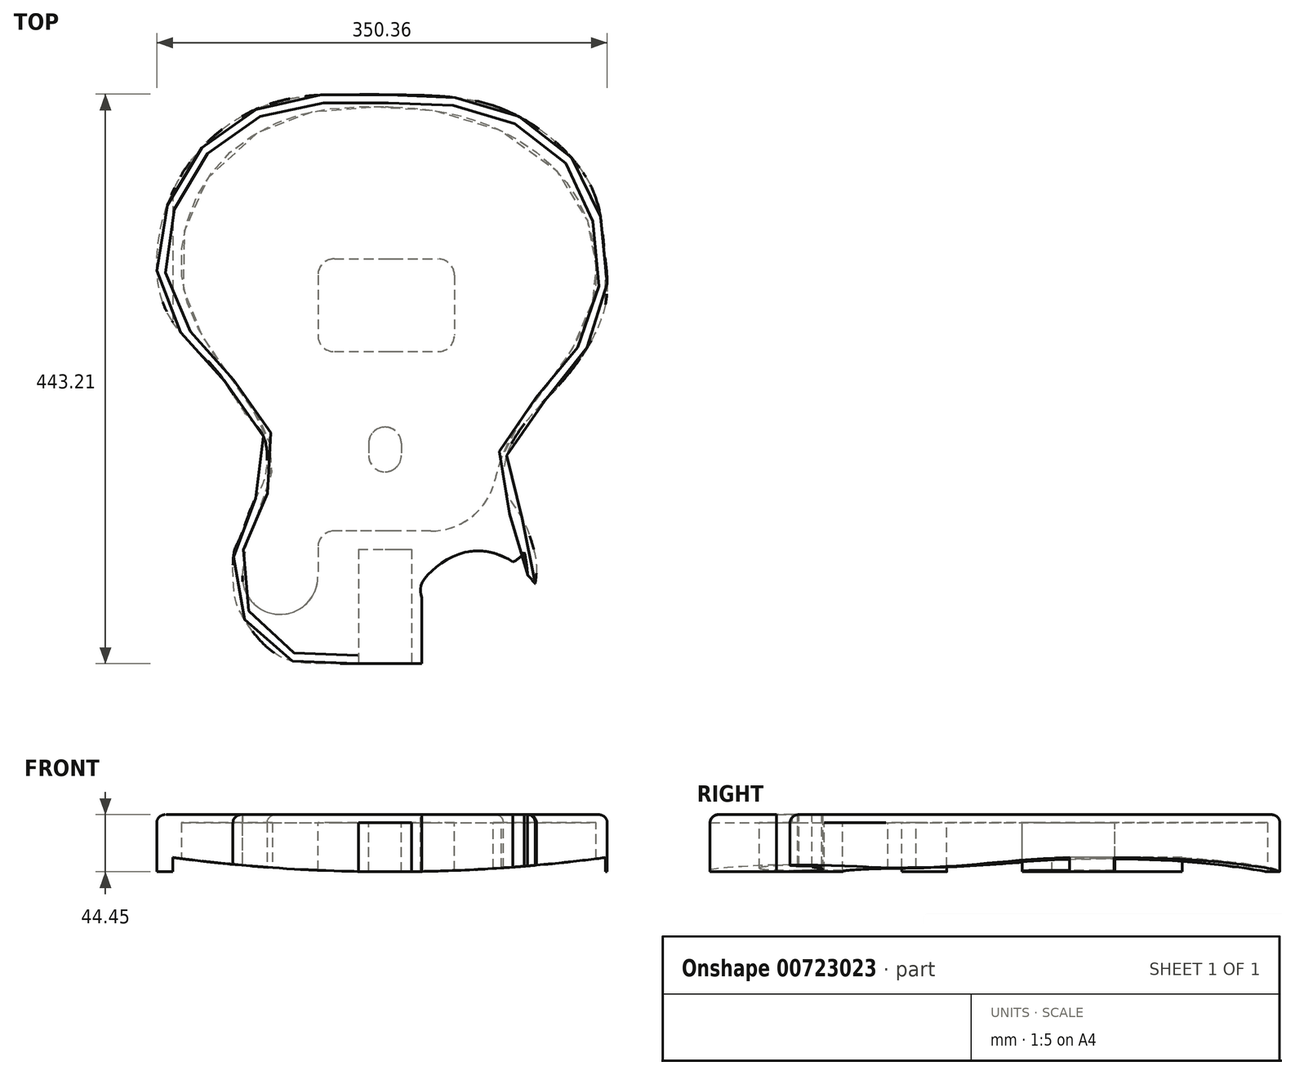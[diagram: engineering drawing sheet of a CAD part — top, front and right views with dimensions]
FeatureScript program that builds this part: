
annotation { "Feature Type Name" : "Feature", "Feature Type Description" : "" }
export const myFeature = defineFeature(function(context is Context, id is Id, definition is map)
    precondition{}
    {
        {
            var Q0;
            Q0=qCreatedBy(makeId("Top.planeOp"),FACE);
            var sketch = newSketch(context, id + "F0", { "sketchPlane" : qUnion([Q0])});
            skFitSpline(sketch, "E0.0", {"points": [v(24.97, -130.68) * mm, v(24.97, -119.75) * mm, v(57.94, -95.86) * mm, v(94.63, -102.44) * mm, v(113.09, -120.18) * mm]});
            skFitSpline(sketch, "E0.1", {"points": [v(-25.03, -182.34) * mm, v(-52.62, -182.34) * mm, v(-87.85, -175.37) * mm, v(-116.14, -142.47) * mm, v(-121.04, -126.28) * mm, v(-121.13, -95.89) * mm, v(-116.63, -84.8) * mm, v(-106.4, -57.9) * mm, v(-97.1, -37.63) * mm, v(-98.08, -5.8) * mm, v(-110.9, 10.46) * mm, v(-135.48, 46.75) * mm, v(-175.53, 96) * mm, v(-165.66, 191.54) * mm, v(-93.42, 253.17) * mm, v(-2.38, 260.37) * mm, v(87.68, 249.3) * mm, v(155.19, 191.74) * mm, v(166.79, 140.27) * mm, v(167.1, 94.3) * mm, v(140.89, 45.49) * mm, v(118.15, 20.01) * mm, v(91.56, -18.26) * mm, v(90.84, -49.26) * mm, v(102.29, -68.12) * mm, v(113.26, -99.56) * mm, v(113.87, -113.65) * mm, v(113.09, -120.18) * mm]});
            skLineSegment(sketch, "E0.2", {"start": v(-24.37, -182.34) * mm, "end": v(16.9, -182.34) * mm});
            skLineSegment(sketch, "E0.3", {"start": v(16.9, -182.34) * mm, "end": v(24.97, -182.34) * mm});
            skLineSegment(sketch, "E0.4", {"start": v(24.97, -182.34) * mm, "end": v(24.97, -130.68) * mm});
            skFitSpline(sketch, "E1.0", {"points": [v(-25.03, -176) * mm, v(-31.98, -176) * mm, v(-42.6, -175.41) * mm, v(-56.36, -173.25) * mm, v(-66.3, -170.9) * mm, v(-75.64, -167.76) * mm, v(-82.78, -164.47) * mm, v(-88.02, -161.43) * mm, v(-91.69, -158.94) * mm, v(-94.52, -156.69) * mm, v(-96.64, -154.78) * mm, v(-98.17, -153.28) * mm, v(-99.64, -151.73) * mm, v(-101.05, -150.13) * mm, v(-102.4, -148.5) * mm, v(-103.66, -146.86) * mm, v(-104.86, -145.22) * mm, v(-106.33, -143.06) * mm, v(-107.96, -140.38) * mm, v(-109.61, -137.19) * mm, v(-111, -133.97) * mm, v(-112.13, -130.69) * mm, v(-113.04, -127.29) * mm, v(-113.74, -123.74) * mm, v(-114.25, -119.99) * mm, v(-114.52, -116.67) * mm, v(-114.64, -113.88) * mm, v(-114.7, -111.75) * mm, v(-114.7, -109.63) * mm, v(-114.66, -107.55) * mm, v(-114.58, -105.56) * mm, v(-114.4, -103.05) * mm, v(-114.06, -100.13) * mm, v(-113.5, -96.87) * mm, v(-112.75, -93.72) * mm, v(-111.84, -90.56) * mm, v(-110.75, -87.3) * mm, v(-109.7, -84.4) * mm, v(-108.77, -81.94) * mm, v(-108.03, -80.01) * mm, v(-107.26, -78) * mm, v(-106.17, -75.17) * mm, v(-105.04, -72.2) * mm, v(-103.84, -69.16) * mm, v(-102.6, -66.08) * mm, v(-100.97, -62.07) * mm, v(-98.95, -57.1) * mm, v(-96.97, -51.98) * mm, v(-95.12, -46.74) * mm, v(-93.78, -42.3) * mm, v(-92.87, -38.72) * mm, v(-92.29, -36) * mm, v(-91.9, -33.74) * mm, v(-91.64, -31.91) * mm, v(-91.5, -30.54) * mm, v(-91.37, -29.17) * mm, v(-91.27, -27.35) * mm, v(-91.22, -25.12) * mm, v(-91.3, -22.5) * mm, v(-91.54, -19.1) * mm, v(-92.1, -15.04) * mm, v(-93.15, -10.43) * mm, v(-94.5, -6.06) * mm, v(-96.14, -1.93) * mm, v(-98.62, 3.3) * mm, v(-101.45, 8.15) * mm, v(-104.46, 12.75) * mm, v(-106.78, 16.11) * mm, v(-108.73, 18.86) * mm, v(-110.27, 21.05) * mm, v(-111.43, 22.69) * mm, v(-112.58, 24.34) * mm, v(-114.12, 26.57) * mm, v(-116.07, 29.4) * mm, v(-118.06, 32.28) * mm, v(-119.68, 34.6) * mm, v(-121.32, 36.93) * mm, v(-123.4, 39.84) * mm, v(-126.72, 44.48) * mm, v(-130.9, 50.3) * mm, v(-135.86, 57.3) * mm, v(-140.63, 64.38) * mm, v(-145.13, 71.54) * mm, v(-149.27, 78.8) * mm, v(-152.94, 86.2) * mm, v(-155.55, 92.47) * mm, v(-157.32, 97.57) * mm, v(-158.87, 102.75) * mm, v(-160.4, 109.38) * mm, v(-161.62, 117.54) * mm, v(-162.2, 125.83) * mm, v(-162.15, 134.2) * mm, v(-161.27, 145.39) * mm, v(-159.17, 156.5) * mm, v(-155.9, 167.28) * mm, v(-152.86, 175.15) * mm, v(-149.27, 182.74) * mm, v(-145.13, 190.01) * mm, v(-140.45, 196.96) * mm, v(-133.56, 205.76) * mm, v(-123.82, 215.85) * mm, v(-112.85, 224.56) * mm, v(-103.48, 230.62) * mm, v(-96.2, 234.7) * mm, v(-88.72, 238.27) * mm, v(-81.08, 241.32) * mm, v(-73.26, 243.89) * mm, v(-62.63, 246.7) * mm, v(-48.97, 249.18) * mm, v(-34.94, 250.5) * mm, v(-23.58, 251) * mm, v(-16.43, 251.12) * mm, v(-10.69, 251.11) * mm, v(-4.94, 251.05) * mm, v(2.22, 250.86) * mm, v(10.78, 250.43) * mm, v(22.12, 249.57) * mm, v(36.12, 247.87) * mm, v(52.58, 244.64) * mm, v(65.94, 240.8) * mm, v(76.37, 236.93) * mm, v(84.06, 233.62) * mm, v(91.62, 229.86) * mm, v(101.47, 224.27) * mm, v(113.24, 216.24) * mm, v(126.07, 205.13) * mm, v(135.38, 194.79) * mm, v(141.8, 185.96) * mm, v(146.08, 179.07) * mm, v(149.76, 171.96) * mm, v(152.85, 164.59) * mm, v(155.4, 156.97) * mm, v(157.4, 149.13) * mm, v(158.66, 142.43) * mm, v(159.42, 136.98) * mm, v(159.87, 132.86) * mm, v(160.15, 129.39) * mm, v(160.32, 126.6) * mm, v(160.45, 123.8) * mm, v(160.53, 120.33) * mm, v(160.47, 116.9) * mm, v(160.31, 114.17) * mm, v(160.08, 111.46) * mm, v(159.64, 108.04) * mm, v(158.87, 103.9) * mm, v(157.9, 99.74) * mm, v(156.72, 95.57) * mm, v(154.92, 90.02) * mm, v(152.25, 83.15) * mm, v(148.57, 75.11) * mm, v(144.54, 67.41) * mm, v(141.03, 61.37) * mm, v(138.22, 56.8) * mm, v(136.13, 53.54) * mm, v(134.07, 50.45) * mm, v(131.38, 46.52) * mm, v(128.06, 41.9) * mm, v(124.02, 36.54) * mm, v(119.8, 31.08) * mm, v(116.03, 26.24) * mm, v(112.82, 22.07) * mm, v(110.3, 18.76) * mm, v(108.1, 15.82) * mm, v(106.26, 13.36) * mm, v(104.38, 10.8) * mm, v(101.93, 7.4) * mm, v(98.95, 3.03) * mm, v(96, -1.63) * mm, v(93.2, -6.57) * mm, v(90.62, -11.77) * mm, v(88.39, -17.25) * mm, v(86.59, -23) * mm, v(85.55, -28) * mm, v(85.05, -32.13) * mm, v(84.87, -35.3) * mm, v(84.9, -38) * mm, v(85.04, -40.19) * mm, v(85.21, -41.84) * mm, v(85.45, -43.49) * mm, v(85.85, -45.66) * mm, v(86.47, -48.34) * mm, v(87.4, -51.5) * mm, v(88.83, -55.64) * mm, v(90.9, -60.7) * mm, v(93.6, -66.64) * mm, v(95.86, -71.48) * mm, v(97.58, -75.28) * mm, v(98.8, -78.1) * mm, v(99.92, -80.87) * mm, v(100.95, -83.64) * mm, v(101.9, -86.4) * mm, v(103.04, -90) * mm, v(104.24, -94.29) * mm, v(105.34, -99.1) * mm, v(106.14, -103.55) * mm, v(106.85, -108.97) * mm, v(107.1, -113.57) * mm, v(107, -117.26) * mm, v(106.86, -118.77) * mm, v(106.78, -119.43) * mm]});
            skLineSegment(sketch, "E2", {"start": v(-3.73, 257.36) * mm, "end": v(-3.73, 314.5) * mm, "construction": true});
            skFitSpline(sketch, "E3.trimOffspring", {"points": [v(-25.03, -176) * mm, v(-31.98, -176) * mm, v(-42.6, -175.41) * mm, v(-56.36, -173.25) * mm, v(-66.3, -170.9) * mm, v(-75.64, -167.76) * mm, v(-82.78, -164.47) * mm, v(-88.02, -161.43) * mm, v(-91.69, -158.94) * mm, v(-94.52, -156.69) * mm, v(-96.64, -154.78) * mm, v(-98.17, -153.28) * mm, v(-99.64, -151.73) * mm, v(-101.05, -150.13) * mm, v(-102.4, -148.5) * mm, v(-103.66, -146.86) * mm, v(-104.86, -145.22) * mm, v(-106.33, -143.06) * mm, v(-107.96, -140.38) * mm, v(-109.61, -137.19) * mm, v(-111, -133.97) * mm, v(-112.13, -130.69) * mm, v(-113.04, -127.29) * mm, v(-113.74, -123.74) * mm, v(-114.25, -119.99) * mm, v(-114.52, -116.67) * mm, v(-114.64, -113.88) * mm, v(-114.7, -111.75) * mm, v(-114.7, -109.63) * mm, v(-114.66, -107.55) * mm, v(-114.58, -105.56) * mm, v(-114.4, -103.05) * mm, v(-114.06, -100.13) * mm, v(-113.5, -96.87) * mm, v(-112.75, -93.72) * mm, v(-111.84, -90.56) * mm, v(-110.75, -87.3) * mm, v(-109.7, -84.4) * mm, v(-108.77, -81.94) * mm, v(-108.03, -80.01) * mm, v(-107.26, -78) * mm, v(-106.17, -75.17) * mm, v(-105.04, -72.2) * mm, v(-103.84, -69.16) * mm, v(-102.6, -66.08) * mm, v(-100.97, -62.07) * mm, v(-98.95, -57.1) * mm, v(-96.97, -51.98) * mm, v(-95.12, -46.74) * mm, v(-93.78, -42.3) * mm, v(-92.87, -38.72) * mm, v(-92.29, -36) * mm, v(-91.9, -33.74) * mm, v(-91.64, -31.91) * mm, v(-91.5, -30.54) * mm, v(-91.37, -29.17) * mm, v(-91.27, -27.35) * mm, v(-91.22, -25.12) * mm, v(-91.3, -22.5) * mm, v(-91.54, -19.1) * mm, v(-92.1, -15.04) * mm, v(-93.15, -10.43) * mm, v(-94.5, -6.06) * mm, v(-96.14, -1.93) * mm, v(-98.62, 3.3) * mm, v(-101.45, 8.15) * mm, v(-104.46, 12.75) * mm, v(-106.78, 16.11) * mm, v(-108.73, 18.86) * mm, v(-110.27, 21.05) * mm, v(-111.43, 22.69) * mm, v(-112.58, 24.34) * mm, v(-114.12, 26.57) * mm, v(-116.07, 29.4) * mm, v(-118.06, 32.28) * mm, v(-119.68, 34.6) * mm, v(-121.32, 36.93) * mm, v(-123.4, 39.84) * mm, v(-126.72, 44.48) * mm, v(-130.9, 50.3) * mm, v(-135.86, 57.3) * mm, v(-140.63, 64.38) * mm, v(-145.13, 71.54) * mm, v(-149.27, 78.8) * mm, v(-152.94, 86.2) * mm, v(-155.55, 92.47) * mm, v(-157.32, 97.57) * mm, v(-158.87, 102.75) * mm, v(-160.4, 109.38) * mm, v(-161.62, 117.54) * mm, v(-162.2, 125.83) * mm, v(-162.15, 134.2) * mm, v(-161.27, 145.39) * mm, v(-159.17, 156.5) * mm, v(-155.9, 167.28) * mm, v(-152.86, 175.15) * mm, v(-149.27, 182.74) * mm, v(-145.13, 190.01) * mm, v(-140.45, 196.96) * mm, v(-133.56, 205.76) * mm, v(-123.82, 215.85) * mm, v(-112.85, 224.56) * mm, v(-103.48, 230.62) * mm, v(-96.2, 234.7) * mm, v(-88.72, 238.27) * mm, v(-81.08, 241.32) * mm, v(-73.26, 243.89) * mm, v(-62.63, 246.7) * mm, v(-48.97, 249.18) * mm, v(-34.94, 250.5) * mm, v(-23.58, 251) * mm, v(-16.43, 251.12) * mm, v(-10.69, 251.11) * mm, v(-4.94, 251.05) * mm, v(2.22, 250.86) * mm, v(10.78, 250.43) * mm, v(22.12, 249.57) * mm, v(36.12, 247.87) * mm, v(52.58, 244.64) * mm, v(65.94, 240.8) * mm, v(76.37, 236.93) * mm, v(84.06, 233.62) * mm, v(91.62, 229.86) * mm, v(101.47, 224.27) * mm, v(113.24, 216.24) * mm, v(126.07, 205.13) * mm, v(135.38, 194.79) * mm, v(141.8, 185.96) * mm, v(146.08, 179.07) * mm, v(149.76, 171.96) * mm, v(152.85, 164.59) * mm, v(155.4, 156.97) * mm, v(157.4, 149.13) * mm, v(158.66, 142.43) * mm, v(159.42, 136.98) * mm, v(159.87, 132.86) * mm, v(160.15, 129.39) * mm, v(160.32, 126.6) * mm, v(160.45, 123.8) * mm, v(160.53, 120.33) * mm, v(160.47, 116.9) * mm, v(160.31, 114.17) * mm, v(160.08, 111.46) * mm, v(159.64, 108.04) * mm, v(158.87, 103.9) * mm, v(157.9, 99.74) * mm, v(156.72, 95.57) * mm, v(154.92, 90.02) * mm, v(152.25, 83.15) * mm, v(148.57, 75.11) * mm, v(144.54, 67.41) * mm, v(141.03, 61.37) * mm, v(138.22, 56.8) * mm, v(136.13, 53.54) * mm, v(134.07, 50.45) * mm, v(131.38, 46.52) * mm, v(128.06, 41.9) * mm, v(124.02, 36.54) * mm, v(119.8, 31.08) * mm, v(116.03, 26.24) * mm, v(112.82, 22.07) * mm, v(110.3, 18.76) * mm, v(108.1, 15.82) * mm, v(106.26, 13.36) * mm, v(104.38, 10.8) * mm, v(101.93, 7.4) * mm, v(98.95, 3.03) * mm, v(96, -1.63) * mm, v(93.2, -6.57) * mm, v(90.62, -11.77) * mm, v(88.39, -17.25) * mm, v(86.59, -23) * mm, v(85.55, -28) * mm, v(85.05, -32.13) * mm, v(84.87, -35.3) * mm, v(84.9, -38) * mm, v(85.04, -40.19) * mm, v(85.21, -41.84) * mm, v(85.45, -43.49) * mm, v(85.85, -45.66) * mm, v(86.47, -48.34) * mm, v(87.4, -51.5) * mm, v(88.83, -55.64) * mm, v(90.9, -60.7) * mm, v(93.6, -66.64) * mm, v(95.86, -71.48) * mm, v(97.58, -75.28) * mm, v(98.8, -78.1) * mm, v(99.92, -80.87) * mm, v(100.95, -83.64) * mm, v(101.9, -86.4) * mm, v(103.04, -90) * mm, v(104.24, -94.29) * mm, v(105.34, -99.1) * mm, v(106.14, -103.55) * mm, v(106.85, -108.97) * mm, v(107.1, -113.57) * mm, v(107, -117.26) * mm, v(106.86, -118.77) * mm, v(106.78, -119.43) * mm]});
            skArc(sketch, "E4.trimOffspring", {"start": v(-38.74, 246.82) * mm, "mid": v(-5.23, 238.32) * mm, "end": v(28.6, 245.5) * mm});
            skPoint(sketch, "E5.visualSharp", {"position": v(33.55, 248.05) * mm});
            skArc(sketch, "E5.filletArc", {"start": v(39.99, 247.01) * mm, "mid": v(34.17, 247.14) * mm, "end": v(28.6, 245.5) * mm});
            skPoint(sketch, "E6.visualSharp", {"position": v(-43.64, 249.6) * mm});
            skArc(sketch, "E6.filletArc", {"start": v(-38.74, 246.82) * mm, "mid": v(-44.33, 248.69) * mm, "end": v(-50.21, 248.76) * mm});
            skArc(sketch, "E7.filletArc", {"start": v(83.94, -104.3) * mm, "mid": v(102.56, -98.18) * mm, "end": v(105.94, -78.87) * mm});
            skLineSegment(sketch, "E8", {"start": v(50.24, -15.3) * mm, "end": v(50.24, 47.77) * mm});
            skArc(sketch, "E9", {"start": v(-55.92, -114.66) * mm, "mid": v(-85.6, -144.02) * mm, "end": v(-114.63, -114.02) * mm});
            skLineSegment(sketch, "E10", {"start": v(-55.92, -114.66) * mm, "end": v(-55.92, -91.8) * mm});
            skLineSegment(sketch, "E11.0.1", {"start": v(50.24, 8.09) * mm, "end": v(-55.92, 8.09) * mm});
            skLineSegment(sketch, "E11.0.7", {"start": v(-55.92, 47.77) * mm, "end": v(50.24, 47.77) * mm});
            skLineSegment(sketch, "E11.1.4", {"start": v(32.86, 47.77) * mm, "end": v(32.86, 8.09) * mm});
            skLineSegment(sketch, "E11.2.2", {"start": v(-39.45, -39.42) * mm, "end": v(31.99, -39.42) * mm});
            skLineSegment(sketch, "E11.2.3", {"start": v(31.99, -39.42) * mm, "end": v(31.99, -79.1) * mm});
            skLineSegment(sketch, "E11.2.8", {"start": v(31.99, -79.1) * mm, "end": v(-43.22, -79.1) * mm});
            skLineSegment(sketch, "E11.3.3", {"start": v(-39.45, -79.1) * mm, "end": v(-39.45, -39.42) * mm});
            skLineSegment(sketch, "E12", {"start": v(-24.37, -182.34) * mm, "end": v(-25.03, -182.34) * mm});
            skLineSegment(sketch, "E13.0.0", {"start": v(-24.37, -93.44) * mm, "end": v(16.9, -93.44) * mm});
            skLineSegment(sketch, "E13.0.1", {"start": v(16.9, -93.44) * mm, "end": v(16.9, -182.34) * mm});
            skLineSegment(sketch, "E13.0.2", {"start": v(16.9, -182.34) * mm, "end": v(-24.37, -182.34) * mm});
            skLineSegment(sketch, "E13.0.3", {"start": v(-24.37, -182.34) * mm, "end": v(-24.37, -93.44) * mm});
            skLineSegment(sketch, "E14", {"start": v(-38.58, 47.77) * mm, "end": v(-38.58, 8.09) * mm});
            skLineSegment(sketch, "E15.0", {"start": v(-43.22, 132.64) * mm, "end": v(37.54, 132.64) * mm});
            skLineSegment(sketch, "E16.0", {"start": v(-43.22, 60.47) * mm, "end": v(37.54, 60.47) * mm});
            skLineSegment(sketch, "E17.trimOffspring", {"start": v(50.24, 73.17) * mm, "end": v(50.24, 119.94) * mm});
            skLineSegment(sketch, "E18.trimOffspring", {"start": v(-55.92, 73.17) * mm, "end": v(-55.92, 119.94) * mm});
            skPoint(sketch, "E19.visualSharp", {"position": v(-55.92, 132.64) * mm});
            skArc(sketch, "E19.filletArc", {"start": v(-43.22, 132.64) * mm, "mid": v(-52.2, 128.92) * mm, "end": v(-55.92, 119.94) * mm});
            skPoint(sketch, "E20.visualSharp", {"position": v(50.24, 132.64) * mm});
            skArc(sketch, "E20.filletArc", {"start": v(50.24, 119.94) * mm, "mid": v(46.52, 128.92) * mm, "end": v(37.54, 132.64) * mm});
            skPoint(sketch, "E21.visualSharp", {"position": v(50.24, 60.47) * mm});
            skArc(sketch, "E21.filletArc", {"start": v(37.54, 60.47) * mm, "mid": v(46.52, 64.2) * mm, "end": v(50.24, 73.17) * mm});
            skPoint(sketch, "E22.visualSharp", {"position": v(-55.92, 60.47) * mm});
            skArc(sketch, "E22.filletArc", {"start": v(-55.92, 73.17) * mm, "mid": v(-52.2, 64.2) * mm, "end": v(-43.22, 60.47) * mm});
            skLineSegment(sketch, "E23.0", {"start": v(-3.73, 1.74) * mm, "end": v(-3.73, 1.74) * mm});
            skLineSegment(sketch, "E24.0", {"start": v(-3.73, -33.07) * mm, "end": v(-3.73, -33.07) * mm});
            skLineSegment(sketch, "E25.0", {"start": v(8.97, -20.37) * mm, "end": v(8.97, -10.96) * mm});
            skLineSegment(sketch, "E26.0", {"start": v(-16.43, -20.37) * mm, "end": v(-16.43, -10.96) * mm});
            skPoint(sketch, "E27.visualSharp", {"position": v(-16.43, 1.74) * mm});
            skArc(sketch, "E27.filletArc", {"start": v(-3.73, 1.74) * mm, "mid": v(-12.71, -1.98) * mm, "end": v(-16.43, -10.96) * mm});
            skPoint(sketch, "E28.visualSharp", {"position": v(8.97, 1.74) * mm});
            skArc(sketch, "E28.filletArc", {"start": v(8.97, -10.96) * mm, "mid": v(5.25, -1.98) * mm, "end": v(-3.73, 1.74) * mm});
            skPoint(sketch, "E29.visualSharp", {"position": v(8.97, -33.07) * mm});
            skArc(sketch, "E29.filletArc", {"start": v(-3.73, -33.07) * mm, "mid": v(5.25, -29.35) * mm, "end": v(8.97, -20.37) * mm});
            skPoint(sketch, "E30.visualSharp", {"position": v(-16.43, -33.07) * mm});
            skArc(sketch, "E30.filletArc", {"start": v(-16.43, -20.37) * mm, "mid": v(-12.71, -29.35) * mm, "end": v(-3.73, -33.07) * mm});
            skArc(sketch, "E31", {"start": v(31.99, -79.1) * mm, "mid": v(61.88, -69.45) * mm, "end": v(80.47, -44.12) * mm});
            skArc(sketch, "E32", {"start": v(88.12, -18.25) * mm, "mid": v(84.02, -31.1) * mm, "end": v(80.47, -44.12) * mm});
            skArc(sketch, "E33.filletArc", {"start": v(-43.22, -79.1) * mm, "mid": v(-52.2, -82.83) * mm, "end": v(-55.92, -91.8) * mm});
            skSolve(sketch);
        }
        {
            var Q0;
            Q0=makeQuery(id+"F0.imprint","IMPRINT",FACE,{"disambiguationData":[TD([[makeQuery(id+"F0.imprint","IMPRINT",EDGE,{"derivedFrom":sQuery(id+"F0.wireOp",EDGE,"E0.0")}),1.0]])]});
            var Q1;
            Q1=makeQuery(id+"F0.imprint","IMPRINT",FACE,{"disambiguationData":[TD([[makeQuery(id+"F0.imprint","IMPRINT",EDGE,{"derivedFrom":sQuery(id+"F0.wireOp",EDGE,"E15.0")}),-1.0]])]});
            var Q2;
            Q2=makeQuery(id+"F0.imprint","IMPRINT",FACE,{"disambiguationData":[TD([[makeQuery(id+"F0.imprint","IMPRINT",EDGE,{"derivedFrom":sQuery(id+"F0.wireOp",EDGE,"E25.0")}),1.0]])]});
            extrude(context, id + "F1", {"entities" : qUnion([Q0, Q1, Q2]), "oppositeDirection" : true, "depth" : 44.45 * mm, "offsetDistance" : 25.4 * mm});
        }
        {
            var Q0;
            Q0=makeQuery(id+"F0.imprint","IMPRINT",FACE,{"disambiguationData":[TD([[makeQuery(id+"F0.imprint","IMPRINT",EDGE,{"derivedFrom":sQuery(id+"F0.wireOp",EDGE,"E1.0")}),-1.0]])]});
            var Q1;
            {var subQ0=sQuery(id+"F0.wireOp",EDGE,"E11.1.4");Q1=makeQuery(id+"F0.imprint","IMPRINT",FACE,{"disambiguationData":[TD([[makeQuery(id+"F0.imprint","IMPRINT",EDGE,{"derivedFrom":subQ0}),-1.0]])]});}
            var Q2;
            Q2=makeQuery(id+"F0.imprint","IMPRINT",FACE,{"disambiguationData":[TD([[makeQuery(id+"F0.imprint","IMPRINT",EDGE,{"derivedFrom":sQuery(id+"F0.wireOp",EDGE,"E11.2.2")}),-1.0]])]});
            var Q3;
            {var subQ5=sQuery(id+"F0.wireOp",EDGE,"E11.1.4");Q3=makeQuery(id+"F0.imprint","IMPRINT",FACE,{"disambiguationData":[TD([[makeQuery(id+"F0.imprint","IMPRINT",EDGE,{"derivedFrom":subQ5}),1.0]])]});}
            var Q4;
            Q4=makeQuery(id+"F0.imprint","IMPRINT",FACE,{"disambiguationData":[TD([[makeQuery(id+"F0.imprint","IMPRINT",EDGE,{"derivedFrom":sQuery(id+"F0.wireOp",EDGE,"E13.0.0")}),-1.0]])]});
            extrude(context, id + "F2", {"entities" : qUnion([Q0, Q1, Q2, Q3, Q4]), "operationType" : NewBodyOperationType.ADD, "oppositeDirection" : true, "depth" : 6.35 * mm, "offsetDistance" : 25.4 * mm});
        }
        {
            var Q0;
            Q0=makeQuery(id+"F1.opExtrude","CAP_EDGE",EDGE,{"disambiguationData":[OSD([sQuery(id+"F0.wireOp",EDGE,"E0.1")])],"isStart":true});
            fillet(context, id + "F3", {"entities" : qUnion([Q0]), "radius" : 6.35 * mm, "tangentPropagation" : true, "allowEdgeOverflow" : false});
        }
        {
            var Q0;
            Q0=makeQuery(id+"F1.opExtrude","SWEPT_FACE",FACE,{"disambiguationData":[OSD([sQuery(id+"F0.wireOp",EDGE,"E13.0.0")])]});
            cPlane(context, id + "F4", {"entities" : qUnion([Q0]), "cplaneType" : CPlaneType.OFFSET, "offset" : 101.6 * mm, "width" : 152.4 * mm, "height" : 152.4 * mm});
        }
        {
            var Q0;
            Q0=qCreatedBy(id+"F4.planeOp",FACE);
            var sketch = newSketch(context, id + "F5", { "sketchPlane" : qUnion([Q0])});
            skLineSegment(sketch, "E34", {"start": v(-3.73, -44.45) * mm, "end": v(-3.73, -102.59) * mm, "construction": true});
            skLineSegment(sketch, "E35", {"start": v(-3.73, -44.45) * mm, "end": v(-3.73, -33.34) * mm, "construction": true});
            skLineSegment(sketch, "E36", {"start": v(-3.73, -33.34) * mm, "end": v(167.72, -33.34) * mm, "construction": true});
            skLineSegment(sketch, "E37", {"start": v(-3.73, -33.34) * mm, "end": v(-168.83, -33.34) * mm, "construction": true});
            skArc(sketch, "E38", {"start": v(-168.83, -33.34) * mm, "mid": v(-0.56, -44.45) * mm, "end": v(167.72, -33.34) * mm});
            skLineSegment(sketch, "E39", {"start": v(-168.83, -33.34) * mm, "end": v(-168.83, -53.41) * mm});
            skLineSegment(sketch, "E40", {"start": v(-168.83, -53.41) * mm, "end": v(167.72, -53.41) * mm});
            skLineSegment(sketch, "E41", {"start": v(167.72, -53.41) * mm, "end": v(167.72, -33.34) * mm});
            skSolve(sketch);
        }
        {
            var Q0;
            Q0=makeQuery(id+"F5.imprint","IMPRINT",FACE,{"disambiguationData":[TD([[makeQuery(id+"F5.imprint","IMPRINT",EDGE,{"derivedFrom":sQuery(id+"F5.wireOp",EDGE,"E38")}),-1.0]])]});
            extrude(context, id + "F6", {"entities" : qUnion([Q0]), "operationType" : NewBodyOperationType.REMOVE, "endBound" : BoundingType.THROUGH_ALL, "oppositeDirection" : true, "depth" : 25.4 * mm, "offsetDistance" : 25.4 * mm});
        }
    });
